# Revit family: PRD_FrankeWS_TltRllHldrs_EXOSToiletRollHolder_EXOS675X
name_source: partatom
category: Specialty Equipment
revit_build: Autodesk Revit 2018 (Build: 20190510_1515(x64)
units: mm (PartAtom-declared; Revit-internal decimal feet)

## family parameters
Cut with Voids When Loaded = No
Host = Face
OmniClass Number = 23.40.20.21.21
OmniClass Title = Toilet Paper Dispensers
Part Type = Normal
Room Calculation Point = No
Round Connector Dimension = Use Diameter
Shared = No

## types (1)
- EXOS675X
    AssetType = Fixed
    BIMObjectName = PRD_AR_ToiletRollHolders_EXOSToiletRollHolder_EXOS675X
    Category = Pr_40_20_76_88, Toilet roll holders
    Default Elevation = 600 mm
    Description = Toilet roll holder for wall mounting, stainless steel with satin finish and InoxPlus surface refinement, material thickness 1.5 mm, for rolls with a maximum diameter of 120 mm, stainless steel spindle with integrated roll stop function, includes mounting materials.
    DurationUnit = year
    Features = stainless steel, surface satin finished
    FillingQuantity = 1
    FillingQuantityUom = Rolls
    Finish = satin finished
    GrossWeight = 0.44 kg
    HolderMaterial = PRD_AR_StainlessSteel_SatinFinished
    IfcExportAs = IfcFurnitureType
    IfcExportType = USERDEFINED
    IntegralAccessories = incl. mounting materials
    IsBuiltIn = TRUE
    Lock = No lock
    MainColor = stainless steel
    Manufacturer = KWC Group AG
    ManufacturerName = KWC Group AG
    ManufacturerURL = www.kwc.com
    Material = stainless steel
    MaterialCode = 1.4301
    MaterialThickness = 1.20 mm
    MaximumDepthDiameterOfConsumable = 120.00 mm
    MaximumWidthOfConsumable = 110.00 mm
    Model = EXOS675X
    ModelNumber = 2030031170
    ModelReference = EXOS675X
    NBSDescription = Toilet roll holders
    NBSReference = 45-35-72/368
    Name = Toilet roll holder EXOS675X
    NetWeight = 0.30 kg
    NominalDepth = 129 mm  [stored 0.423228 ft]
    NominalHeight = 62 mm  [stored 0.203412 ft]
    NominalWidth = 123 mm  [stored 0.403543 ft]
    ProductInformation = https://pim.kwc.com
    Size = 123 x 62 x 129 mm
    Spindle = Yes
    Style = Roll holder
    SurfaceTreatment = InoxPlus (anti fingerprint)
    ToiletRollMaterial = PRD_AR_ToiletRoll
    TypeOfFixing = Screw
    TypeOfMounting = Wall mounting
    URL = www.kwc.com
    Uniclass2015Code = Pr_40_20_76_88
    Uniclass2015Title = Toilet roll holders
    Uniclass2015Version = Products v1.17
    Version = 1
    WarrantyDurationUnit = year

note: [stored X ft] marks values corroborated as IEEE doubles in the binary element streams (Revit-internal decimal feet)

## geometry (parser evidence)
native form markers: Sweep x2
no freeform markers — native parametric forms only
